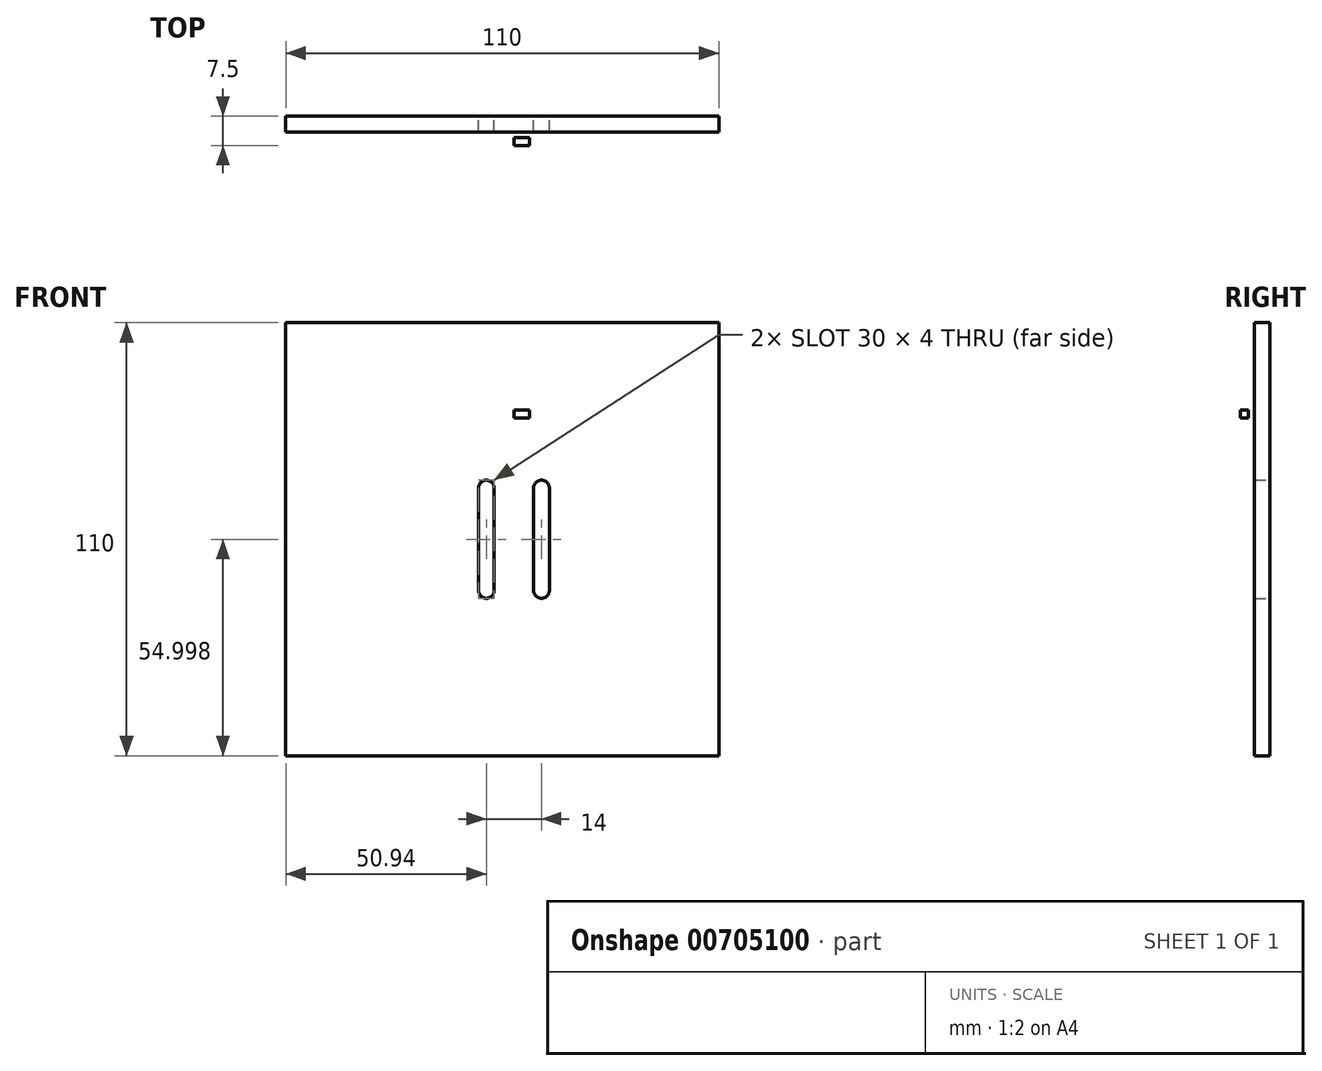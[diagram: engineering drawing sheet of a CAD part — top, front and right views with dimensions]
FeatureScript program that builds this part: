
annotation { "Feature Type Name" : "Feature", "Feature Type Description" : "" }
export const myFeature = defineFeature(function(context is Context, id is Id, definition is map)
    precondition{}
    {
        {
            var Q0;
            Q0=qCreatedBy(makeId("Front.planeOp"),FACE);
            var sketch = newSketch(context, id + "F0", { "sketchPlane" : qUnion([Q0])});
            skLineSegment(sketch, "E0.bottom", {"start": v(-57.94, 58.18) * mm, "end": v(52.06, 58.18) * mm});
            skLineSegment(sketch, "E0.top", {"start": v(-57.94, -51.82) * mm, "end": v(52.06, -51.82) * mm});
            skLineSegment(sketch, "E0.left", {"start": v(-57.94, 58.18) * mm, "end": v(-57.94, -51.82) * mm});
            skLineSegment(sketch, "E0.right", {"start": v(52.06, 58.18) * mm, "end": v(52.06, -51.82) * mm});
            skLineSegment(sketch, "E1.bottom", {"start": v(5, 16.18) * mm, "end": v(9, 16.18) * mm});
            skLineSegment(sketch, "E1.top", {"start": v(5, -9.82) * mm, "end": v(9, -9.82) * mm});
            skLineSegment(sketch, "E1.left", {"start": v(5, 16.18) * mm, "end": v(5, -9.82) * mm});
            skLineSegment(sketch, "E1.right", {"start": v(9, 16.18) * mm, "end": v(9, -9.82) * mm});
            skLineSegment(sketch, "E2.MirrorCS", {"start": v(-5, 16.18) * mm, "end": v(-9, 16.18) * mm});
            skLineSegment(sketch, "E3.MirrorCS", {"start": v(-5, 16.18) * mm, "end": v(-5, -9.82) * mm});
            skLineSegment(sketch, "E4.MirrorCS", {"start": v(-9, 16.18) * mm, "end": v(-9, -9.82) * mm});
            skLineSegment(sketch, "E5.MirrorCS", {"start": v(-5, -9.82) * mm, "end": v(-9, -9.82) * mm});
            skPoint(sketch, "E6.third.point.positionSnap0", {"position": v(-7, 16.18) * mm});
            skArc(sketch, "E7", {"start": v(9, 16.18) * mm, "mid": v(7, 18.18) * mm, "end": v(5, 16.18) * mm});
            skArc(sketch, "E8", {"start": v(5, -9.82) * mm, "mid": v(7, -11.82) * mm, "end": v(9, -9.82) * mm});
            skArc(sketch, "E9", {"start": v(-5, 16.18) * mm, "mid": v(-7, 18.18) * mm, "end": v(-9, 16.18) * mm});
            skArc(sketch, "E10", {"start": v(-9, -9.82) * mm, "mid": v(-7, -11.82) * mm, "end": v(-5, -9.82) * mm});
            skSolve(sketch);
        }
        {
            var Q0;
            Q0=makeQuery(id+"F0.imprint","IMPRINT",FACE,{"disambiguationData":[TD([[makeQuery(id+"F0.imprint","IMPRINT",EDGE,{"derivedFrom":sQuery(id+"F0.wireOp",EDGE,"E0.bottom")}),-1.0]])]});
            extrude(context, id + "F1", {"entities" : qUnion([Q0]), "depth" : 4 * mm, "offsetDistance" : 25 * mm});
        }
        {
            var Q0;
            Q0=qCreatedBy(makeId("Right.planeOp"),FACE);
            var sketch = newSketch(context, id + "F2", { "sketchPlane" : qUnion([Q0])});
            skLineSegment(sketch, "E11.bottom", {"start": v(-55.5, 35.97) * mm, "end": v(-5.5, 35.97) * mm});
            skLineSegment(sketch, "E11.top", {"start": v(-55.5, 5.97) * mm, "end": v(-5.5, 5.97) * mm});
            skLineSegment(sketch, "E11.left", {"start": v(-55.5, 35.97) * mm, "end": v(-55.5, 5.97) * mm});
            skLineSegment(sketch, "E11.right", {"start": v(-5.5, 35.97) * mm, "end": v(-5.5, 5.97) * mm});
            skLineSegment(sketch, "E12.bottom", {"start": v(-7.5, 5.97) * mm, "end": v(-5.5, 5.97) * mm});
            skLineSegment(sketch, "E12.top", {"start": v(-7.5, 7.97) * mm, "end": v(-5.5, 7.97) * mm});
            skLineSegment(sketch, "E12.left", {"start": v(-7.5, 5.97) * mm, "end": v(-7.5, 7.97) * mm});
            skLineSegment(sketch, "E12.right", {"start": v(-5.5, 5.97) * mm, "end": v(-5.5, 7.97) * mm});
            skLineSegment(sketch, "E13.bottom", {"start": v(-7.5, 35.97) * mm, "end": v(-5.5, 35.97) * mm});
            skLineSegment(sketch, "E13.top", {"start": v(-7.5, 33.97) * mm, "end": v(-5.5, 33.97) * mm});
            skLineSegment(sketch, "E13.left", {"start": v(-7.5, 35.97) * mm, "end": v(-7.5, 33.97) * mm});
            skLineSegment(sketch, "E13.right", {"start": v(-5.5, 35.97) * mm, "end": v(-5.5, 33.97) * mm});
            skSolve(sketch);
        }
        {
            var Q0;
            Q0=makeQuery(id+"F2.imprint","IMPRINT",FACE,{"disambiguationData":[TD([[makeQuery(id+"F2.imprint","IMPRINT",EDGE,{"derivedFrom":sQuery(id+"F2.wireOp",EDGE,"E11.bottom")}),-1.0]])]});
            extrude(context, id + "F3", {"entities" : qUnion([Q0]), "depth" : 4 * mm, "offsetDistance" : 25 * mm});
        }
    });
